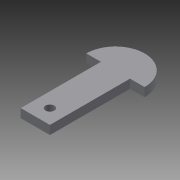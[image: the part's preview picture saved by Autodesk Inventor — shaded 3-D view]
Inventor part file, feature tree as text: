
AUTODESK INVENTOR PART (.ipt)
format: ipt  version: 2015 SP2 (Build 190223200, 223)  size: 85,504 bytes
history: native  units: in
note: dims shown in document units (in); Inventor stores cm internally (conversion verified against a paired STEP export)
features: sketch x2, extrude x1, hole x1
ambient origin geometry x8: Origin, YZ Plane, XZ Plane, XY Plane, X Axis, Y Axis, Z Axis, Center Point
bodies: Solid1 (feature_tree)
feature tree (4):
  extrude  "Extrusion1"  Depth=1.0827in
  hole  "Hole1"  [1 undecoded]
  sketch  "Sketch1"  dims[d0=0.3937in d1=1.0827in]
  sketch  "Sketch2"  dims[d2=0.1969in d3=0.1969in d4=0.1181in d5=0.0in d6=0.1181in d7=0.1969in d8=0.1969in d9=0.1181in d10=0.2362in d11=0.1575in d12=0.0787in d13=90.0deg d14=0.315in d15=0.8108in]
note: 1 required parameter value undecoded (feature->parameter linkage not recoverable at this tier; creation-order binding heuristic only, values carry confidence <= 0.55)
